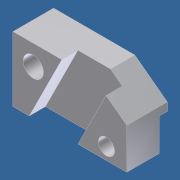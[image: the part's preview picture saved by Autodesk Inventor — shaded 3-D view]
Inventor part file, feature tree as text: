
AUTODESK INVENTOR PART (.ipt)
format: ipt  version: unknown  size: 210,944 bytes
history: native  units: in
note: dims shown in document units (in); Inventor stores cm internally (conversion verified against a paired STEP export)
features: sketch x6, extrude x4, hole x2
ambient origin geometry x8: Origin, YZ Plane, XZ Plane, XY Plane, X Axis, Y Axis, Z Axis, Center Point
bodies: Solid1 (feature_tree)
feature tree (12):
  extrude  "Extrusion1"  Depth=4.0in
  extrude  "Extrusion2"  Depth=3.0in
  extrude  "Extrusion3"  Depth=1.0in
  extrude  "Extrusion4"  Depth=1.0in TaperAngle=0.0deg
  hole  "Hole1"  [1 undecoded]
  hole  "Hole2"  [1 undecoded]
  sketch  "Sketch1"  dims[d0=7.0in d1=4.0in]
  sketch  "Sketch2"  dims[d2=2.5in d3=0.0in d4=3.0in]
  sketch  "Sketch3"  dims[d5=1.0in d6=1.0in]
  sketch  "Sketch4"  dims[d7=3.0in d8=1.0in d9=0.0in]
  sketch  "Sketch5"  dims[d10=2.0in d11=1.5in]
  sketch  "Sketch6"  dims[d12=1.0in d13=0.0in d14=0.5in d15=2.0in d16=1.0in d17=0.0in d18=1.25in d19=0.75in d20=1.0in d21=0.75in d22=0.375in d23=0.25in d24=0.5635in d25=1.0in d26=0.8108in d27=1.25in d28=1.25in d29=1.25in d30=0.75in d31=0.375in d32=0.25in d33=0.5635in d34=1.0in d35=0.0in]
note: 2 required parameter values undecoded (feature->parameter linkage not recoverable at this tier; creation-order binding heuristic only, values carry confidence <= 0.55)
